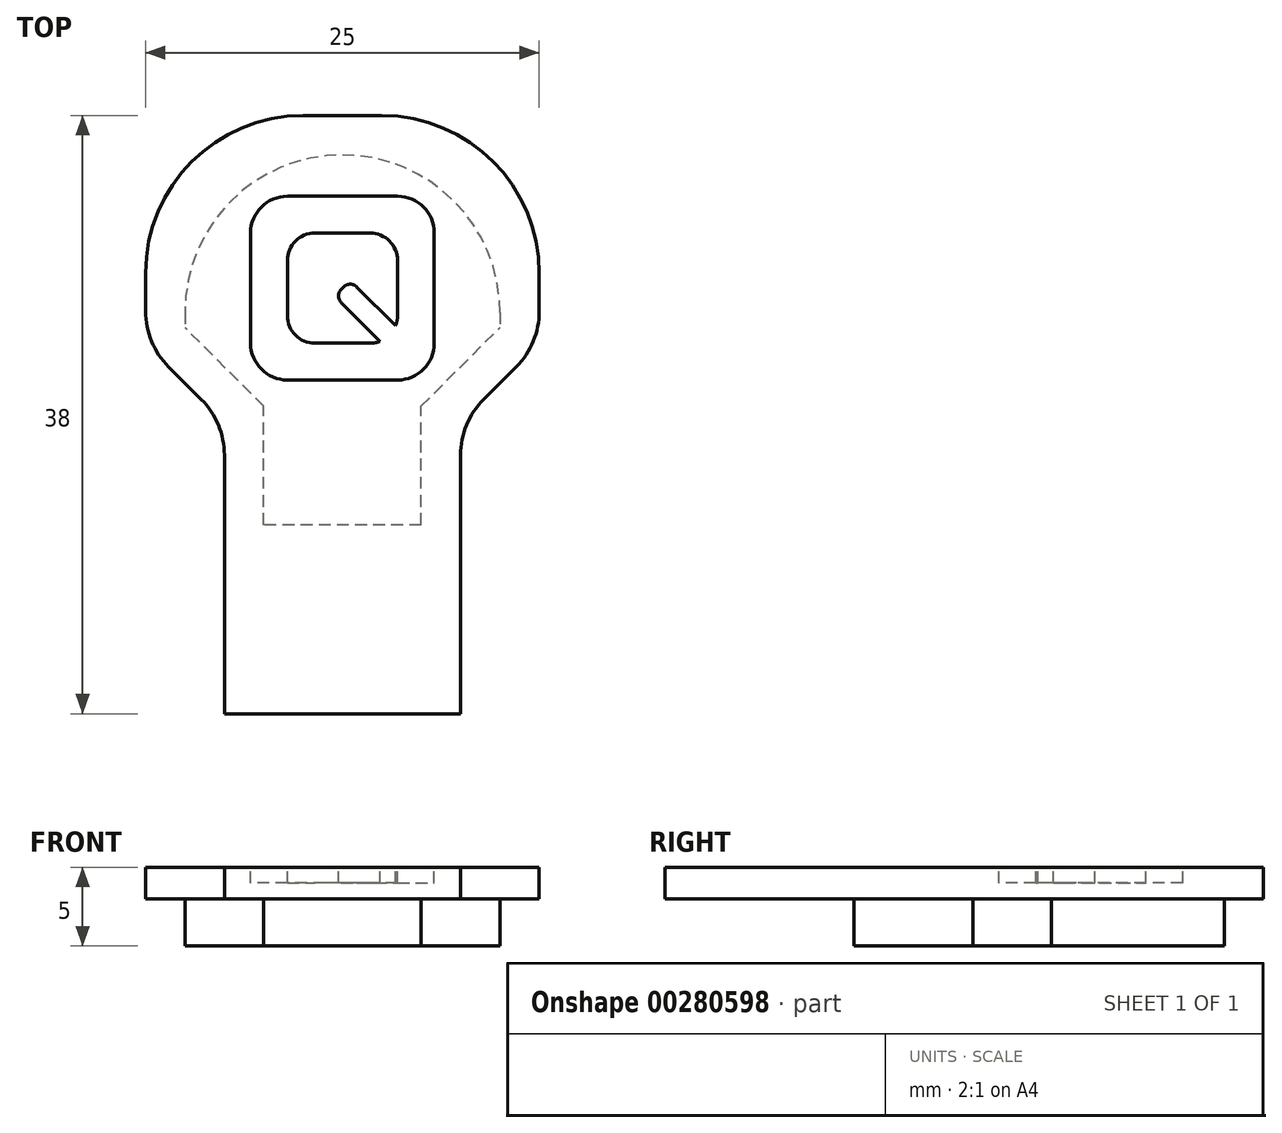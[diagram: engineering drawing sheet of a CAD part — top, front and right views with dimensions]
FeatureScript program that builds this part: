
annotation { "Feature Type Name" : "Feature", "Feature Type Description" : "" }
export const myFeature = defineFeature(function(context is Context, id is Id, definition is map)
    precondition{}
    {
        {
            var Q0;
            Q0=qCreatedBy(makeId("Top.planeOp"),FACE);
            var sketch = newSketch(context, id + "F0", { "sketchPlane" : qUnion([Q0])});
            skLineSegment(sketch, "E0", {"start": v(0, 0) * mm, "end": v(7.5, 0) * mm});
            skLineSegment(sketch, "E1", {"start": v(7.5, 0) * mm, "end": v(7.5, 12.43) * mm});
            skLineSegment(sketch, "E2", {"start": v(7.5, 14.5) * mm, "end": v(12.5, 14.5) * mm, "construction": true});
            skLineSegment(sketch, "E3", {"start": v(12.5, 14.5) * mm, "end": v(12.5, 19.5) * mm, "construction": true});
            skLineSegment(sketch, "E4", {"start": v(8.96, 15.96) * mm, "end": v(11.04, 18.04) * mm});
            skLineSegment(sketch, "E5", {"start": v(12.5, 24) * mm, "end": v(12.5, 21.57) * mm});
            skLineSegment(sketch, "E6", {"start": v(2.5, 34) * mm, "end": v(0, 34) * mm});
            skLineSegment(sketch, "E7.MirrorCS", {"start": v(-7.5, 14.5) * mm, "end": v(-12.5, 14.5) * mm, "construction": true});
            skLineSegment(sketch, "E8.MirrorCS", {"start": v(-12.5, 14.5) * mm, "end": v(-12.5, 19.5) * mm, "construction": true});
            skLineSegment(sketch, "E9.MirrorCS", {"start": v(-12.5, 24) * mm, "end": v(-12.5, 21.57) * mm});
            skLineSegment(sketch, "E10.MirrorCS", {"start": v(0, 0) * mm, "end": v(-7.5, 0) * mm});
            skLineSegment(sketch, "E11.MirrorCS", {"start": v(-7.5, 0) * mm, "end": v(-7.5, 12.43) * mm});
            skLineSegment(sketch, "E12.MirrorCS", {"start": v(-2.5, 34) * mm, "end": v(0, 34) * mm});
            skLineSegment(sketch, "E13.MirrorCS", {"start": v(-8.96, 15.96) * mm, "end": v(-11.04, 18.04) * mm});
            skLineSegment(sketch, "E14.2", {"start": v(0, 31.5) * mm, "end": v(0, 31.5) * mm});
            skLineSegment(sketch, "E14.6", {"start": v(0, 31.5) * mm, "end": v(0, 31.5) * mm});
            skPoint(sketch, "E15.orphan", {"position": v(-5, 0.46) * mm});
            skPoint(sketch, "E16.orphan", {"position": v(5, 0.46) * mm});
            skPoint(sketch, "E17.visualSharp", {"position": v(-10, 31.5) * mm});
            skPoint(sketch, "E18.visualSharp", {"position": v(10, 31.5) * mm});
            skPoint(sketch, "E19.visualSharp", {"position": v(-12.5, 19.5) * mm});
            skArc(sketch, "E19.filletArc", {"start": v(-12.5, 21.57) * mm, "mid": v(-12.12, 19.66) * mm, "end": v(-11.04, 18.04) * mm});
            skPoint(sketch, "E20.visualSharp", {"position": v(-7.5, 14.5) * mm});
            skArc(sketch, "E20.filletArc", {"start": v(-7.5, 12.43) * mm, "mid": v(-7.88, 14.34) * mm, "end": v(-8.96, 15.96) * mm});
            skPoint(sketch, "E21.visualSharp", {"position": v(7.5, 14.5) * mm});
            skArc(sketch, "E21.filletArc", {"start": v(8.96, 15.96) * mm, "mid": v(7.88, 14.34) * mm, "end": v(7.5, 12.43) * mm});
            skPoint(sketch, "E22.visualSharp", {"position": v(12.5, 19.5) * mm});
            skArc(sketch, "E22.filletArc", {"start": v(11.04, 18.04) * mm, "mid": v(12.12, 19.66) * mm, "end": v(12.5, 21.57) * mm});
            skPoint(sketch, "E23.visualSharp", {"position": v(-12.5, 34) * mm});
            skArc(sketch, "E23.filletArc", {"start": v(-2.5, 34) * mm, "mid": v(-9.57, 31.07) * mm, "end": v(-12.5, 24) * mm});
            skPoint(sketch, "E24.visualSharp", {"position": v(12.5, 34) * mm});
            skArc(sketch, "E24.filletArc", {"start": v(12.5, 24) * mm, "mid": v(9.57, 31.07) * mm, "end": v(2.5, 34) * mm});
            skSolve(sketch);
        }
        {
            var Q0;
            Q0=makeQuery(id+"F0.imprint","IMPRINT",FACE,{"disambiguationData":[TD([[makeQuery(id+"F0.imprint","IMPRINT",EDGE,{"derivedFrom":sQuery(id+"F0.wireOp",EDGE,"E0")}),1.0]])]});
            extrude(context, id + "F1", {"entities" : qUnion([Q0]), "depth" : 2 * mm});
        }
        {
            var Q0;
            Q0=makeQuery(id+"F1.opExtrude","CAP_FACE",FACE,{"disambiguationData":[OSD([sQuery(id+"F0.wireOp",EDGE,"E0"),sQuery(id+"F0.wireOp",EDGE,"E1"),sQuery(id+"F0.wireOp",EDGE,"E4"),sQuery(id+"F0.wireOp",EDGE,"E5"),sQuery(id+"F0.wireOp",EDGE,"E6"),sQuery(id+"F0.wireOp",EDGE,"E9.MirrorCS"),sQuery(id+"F0.wireOp",EDGE,"E10.MirrorCS"),sQuery(id+"F0.wireOp",EDGE,"E11.MirrorCS"),sQuery(id+"F0.wireOp",EDGE,"E12.MirrorCS"),sQuery(id+"F0.wireOp",EDGE,"E13.MirrorCS"),sQuery(id+"F0.wireOp",EDGE,"E19.filletArc"),sQuery(id+"F0.wireOp",EDGE,"E20.filletArc"),sQuery(id+"F0.wireOp",EDGE,"E21.filletArc"),sQuery(id+"F0.wireOp",EDGE,"E22.filletArc"),sQuery(id+"F0.wireOp",EDGE,"E23.filletArc"),sQuery(id+"F0.wireOp",EDGE,"E24.filletArc")])],"isStart":true});
            var sketch = newSketch(context, id + "F2", { "sketchPlane" : qUnion([Q0])});
            skLineSegment(sketch, "E25.0", {"start": v(10, -21.5) * mm, "end": v(10, -20.54) * mm});
            skLineSegment(sketch, "E25.1", {"start": v(5, -15.54) * mm, "end": v(10, -20.54) * mm});
            skLineSegment(sketch, "E25.3", {"start": v(5, -8) * mm, "end": v(5, -15.54) * mm});
            skLineSegment(sketch, "E25.7", {"start": v(-10, -21.5) * mm, "end": v(-10, -20.54) * mm});
            skLineSegment(sketch, "E25.8", {"start": v(-5, -15.54) * mm, "end": v(-10, -20.54) * mm});
            skLineSegment(sketch, "E25.9", {"start": v(-5, -8) * mm, "end": v(-5, -15.54) * mm});
            skLineSegment(sketch, "E26", {"start": v(5, -8) * mm, "end": v(-5, -8) * mm});
            skArc(sketch, "E27.filletArc", {"start": v(0, -31.5) * mm, "mid": v(7.07, -28.57) * mm, "end": v(10, -21.5) * mm});
            skArc(sketch, "E28.filletArc", {"start": v(-10, -21.5) * mm, "mid": v(-7.07, -28.57) * mm, "end": v(0, -31.5) * mm});
            skSolve(sketch);
        }
        {
            var Q0;
            Q0=makeQuery(id+"F2.imprint","IMPRINT",FACE,{"disambiguationData":[TD([[makeQuery(id+"F2.imprint","IMPRINT",EDGE,{"derivedFrom":sQuery(id+"F2.wireOp",EDGE,"E25.0")}),1.0]])]});
            extrude(context, id + "F3", {"entities" : qUnion([Q0]), "operationType" : NewBodyOperationType.ADD, "depth" : 3 * mm});
        }
        {
            var Q0;
            Q0=makeQuery(id+"F1.opExtrude","SWEPT_FACE",FACE,{"disambiguationData":[OSD([sQuery(id+"F0.wireOp",EDGE,"E0"),sQuery(id+"F0.wireOp",EDGE,"E10.MirrorCS")])]});
            var sketch = newSketch(context, id + "F4", { "sketchPlane" : qUnion([Q0])});
            skLineSegment(sketch, "E29", {"start": v(-7.5, 2) * mm, "end": v(7.5, 2) * mm});
            skLineSegment(sketch, "E30", {"start": v(7.5, 2) * mm, "end": v(7.5, 0) * mm});
            skLineSegment(sketch, "E31", {"start": v(7.5, 0) * mm, "end": v(-7.5, 0) * mm});
            skLineSegment(sketch, "E32", {"start": v(-7.5, 0) * mm, "end": v(-7.5, 2) * mm});
            skSolve(sketch);
        }
        {
            var Q0;
            Q0=makeQuery(id+"F4.imprint","IMPRINT",FACE,{"disambiguationData":[TD([[makeQuery(id+"F4.imprint","IMPRINT",EDGE,{"derivedFrom":sQuery(id+"F4.wireOp",EDGE,"E29")}),1.0]])]});
            extrude(context, id + "F5", {"entities" : qUnion([Q0]), "operationType" : NewBodyOperationType.ADD, "depth" : 4 * mm});
        }
        {
            var Q0;
            Q0=makeQuery(id+"F5.boolean.opBoolean","MERGE",FACE,{"derivedFrom":[makeQuery(id+"F1.opExtrude","CAP_FACE",FACE,{"disambiguationData":[OSD([sQuery(id+"F0.wireOp",EDGE,"E0"),sQuery(id+"F0.wireOp",EDGE,"E1"),sQuery(id+"F0.wireOp",EDGE,"E4"),sQuery(id+"F0.wireOp",EDGE,"E5"),sQuery(id+"F0.wireOp",EDGE,"E6"),sQuery(id+"F0.wireOp",EDGE,"E9.MirrorCS"),sQuery(id+"F0.wireOp",EDGE,"E10.MirrorCS"),sQuery(id+"F0.wireOp",EDGE,"E11.MirrorCS"),sQuery(id+"F0.wireOp",EDGE,"E12.MirrorCS"),sQuery(id+"F0.wireOp",EDGE,"E13.MirrorCS"),sQuery(id+"F0.wireOp",EDGE,"E19.filletArc"),sQuery(id+"F0.wireOp",EDGE,"E20.filletArc"),sQuery(id+"F0.wireOp",EDGE,"E21.filletArc"),sQuery(id+"F0.wireOp",EDGE,"E22.filletArc"),sQuery(id+"F0.wireOp",EDGE,"E23.filletArc"),sQuery(id+"F0.wireOp",EDGE,"E24.filletArc")])],"isStart":false}),makeQuery(id+"F5.opExtrude","SWEPT_FACE",FACE,{"disambiguationData":[OSD([sQuery(id+"F4.wireOp",EDGE,"E29")])]})]});
            var sketch = newSketch(context, id + "F6", { "sketchPlane" : qUnion([Q0])});
            skLineSegment(sketch, "E33", {"start": v(0, 23.12) * mm, "end": v(0, 23.04) * mm, "construction": true});
            skLineSegment(sketch, "E34", {"start": v(-3.5, 17.2) * mm, "end": v(3.5, 17.2) * mm});
            skLineSegment(sketch, "E35", {"start": v(5.83, 19.54) * mm, "end": v(5.83, 26.54) * mm});
            skLineSegment(sketch, "E36", {"start": v(3.5, 28.87) * mm, "end": v(-3.5, 28.87) * mm});
            skLineSegment(sketch, "E37", {"start": v(-5.83, 26.54) * mm, "end": v(-5.83, 19.54) * mm});
            skArc(sketch, "E38", {"start": v(-3.5, 28.87) * mm, "mid": v(-5.15, 28.19) * mm, "end": v(-5.83, 26.54) * mm});
            skArc(sketch, "E39", {"start": v(5.83, 26.54) * mm, "mid": v(5.15, 28.19) * mm, "end": v(3.5, 28.87) * mm});
            skArc(sketch, "E40", {"start": v(-5.83, 19.54) * mm, "mid": v(-5.15, 17.89) * mm, "end": v(-3.5, 17.2) * mm});
            skArc(sketch, "E41", {"start": v(3.5, 17.2) * mm, "mid": v(5.15, 17.89) * mm, "end": v(5.83, 19.54) * mm});
            skLineSegment(sketch, "E42", {"start": v(-1.75, 19.54) * mm, "end": v(1.75, 19.54) * mm});
            skLineSegment(sketch, "E43", {"start": v(3.5, 21.29) * mm, "end": v(3.5, 24.79) * mm});
            skLineSegment(sketch, "E44", {"start": v(1.75, 26.54) * mm, "end": v(-1.75, 26.54) * mm});
            skLineSegment(sketch, "E45", {"start": v(-3.5, 24.79) * mm, "end": v(-3.5, 21.29) * mm});
            skArc(sketch, "E46", {"start": v(-1.75, 26.54) * mm, "mid": v(-2.99, 26.02) * mm, "end": v(-3.5, 24.79) * mm});
            skArc(sketch, "E47", {"start": v(3.5, 24.79) * mm, "mid": v(2.99, 26.02) * mm, "end": v(1.75, 26.54) * mm});
            skArc(sketch, "E48", {"start": v(-3.5, 21.29) * mm, "mid": v(-2.99, 20.05) * mm, "end": v(-1.75, 19.54) * mm});
            skLineSegment(sketch, "E49", {"start": v(0, 23.04) * mm, "end": v(0.08, 23.12) * mm});
            skLineSegment(sketch, "E50", {"start": v(0.9, 23.12) * mm, "end": v(3.38, 20.65) * mm});
            skLineSegment(sketch, "E51", {"start": v(-0.08, 22.13) * mm, "end": v(2.39, 19.66) * mm});
            skArc(sketch, "E52", {"start": v(0.9, 23.12) * mm, "mid": v(0.5, 23.29) * mm, "end": v(0.08, 23.12) * mm});
            skArc(sketch, "E53", {"start": v(-0.08, 22.95) * mm, "mid": v(-0.25, 22.54) * mm, "end": v(-0.08, 22.13) * mm});
            skArc(sketch, "E54", {"start": v(1.75, 19.54) * mm, "mid": v(2.08, 19.57) * mm, "end": v(2.39, 19.66) * mm});
            skArc(sketch, "E55", {"start": v(3.38, 20.65) * mm, "mid": v(3.47, 20.96) * mm, "end": v(3.5, 21.29) * mm});
            skLineSegment(sketch, "E56", {"start": v(-0.08, 22.95) * mm, "end": v(0, 23.04) * mm});
            skSolve(sketch);
        }
        {
            var Q0;
            Q0 = qSketchRegion(id + "F6", true);
            extrude(context, id + "F7", {"entities" : qUnion([Q0]), "operationType" : NewBodyOperationType.REMOVE, "oppositeDirection" : true, "depth" : 1 * mm});
        }
    });
